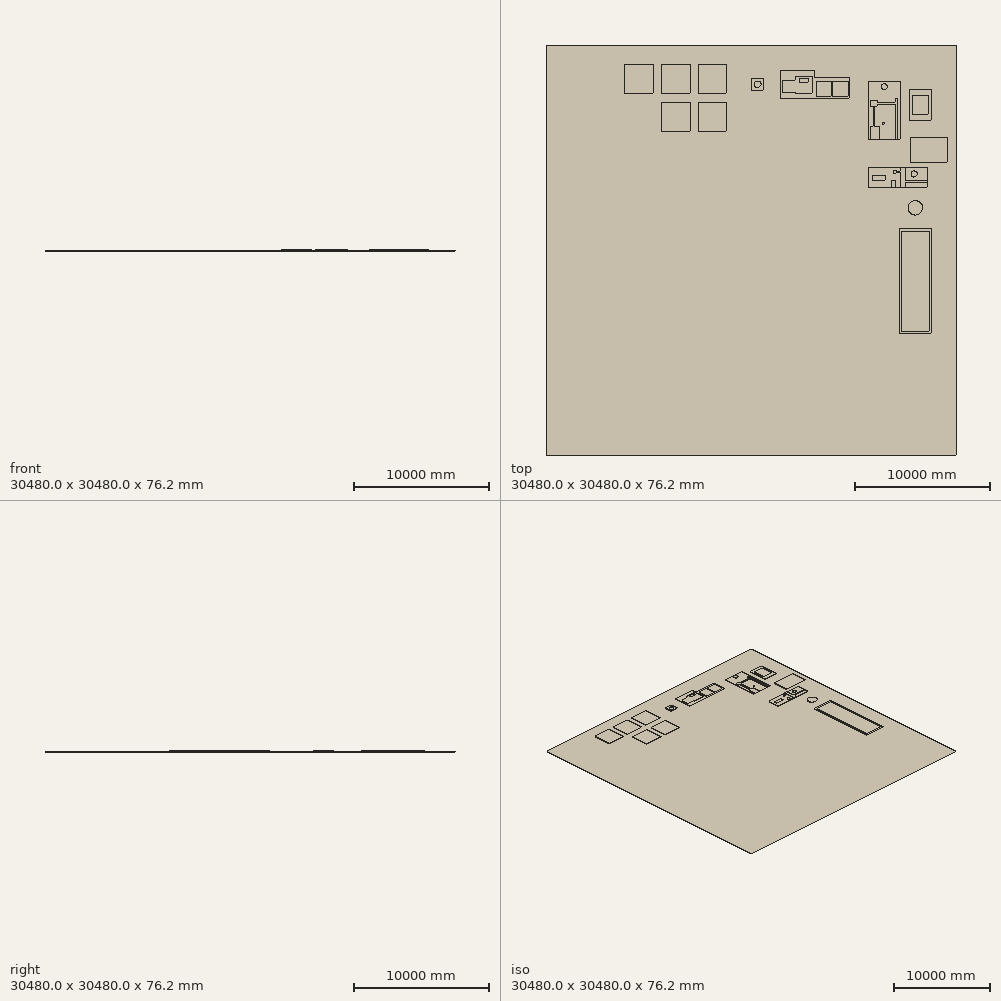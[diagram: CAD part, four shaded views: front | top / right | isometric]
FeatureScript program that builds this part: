
annotation { "Feature Type Name" : "Feature", "Feature Type Description" : "" }
export const myFeature = defineFeature(function(context is Context, id is Id, definition is map)
    precondition{}
    {
        {
            var Q0;
            Q0=qCreatedBy(makeId("Top.planeOp"),FACE);
            var sketch = newSketch(context, id + "F0", { "sketchPlane" : qUnion([Q0])});
            skLineSegment(sketch, "E0.bottom", {"start": v(15240, 15240) * mm, "end": v(-15240, 15240) * mm});
            skLineSegment(sketch, "E0.top", {"start": v(15240, -15240) * mm, "end": v(-15240, -15240) * mm});
            skLineSegment(sketch, "E0.left", {"start": v(15240, 15240) * mm, "end": v(15240, -15240) * mm});
            skLineSegment(sketch, "E0.right", {"start": v(-15240, 15240) * mm, "end": v(-15240, -15240) * mm});
            skPoint(sketch, "E0.middle", {"position": v(0, 0) * mm});
            skSolve(sketch);
        }
        {
            var Q0;
            Q0 = qSketchRegion(id + "F0", true);
            extrude(context, id + "F1", {"entities" : qUnion([Q0]), "depth" : 25.4 * mm, "offsetDistance" : 25.4 * mm});
        }
        {
            var Q0;
            Q0=makeQuery(id+"F1.opExtrude","CAP_FACE",FACE,{"disambiguationData":[OSD([sQuery(id+"F0.wireOp",EDGE,"E0.bottom"),sQuery(id+"F0.wireOp",EDGE,"E0.top"),sQuery(id+"F0.wireOp",EDGE,"E0.left"),sQuery(id+"F0.wireOp",EDGE,"E0.right")])],"isStart":false});
            var sketch = newSketch(context, id + "F2", { "sketchPlane" : qUnion([Q0])});
            skLineSegment(sketch, "E1.bottom", {"start": v(2133.6, 12852.4) * mm, "end": v(7315.2, 12852.4) * mm});
            skLineSegment(sketch, "E1.top", {"start": v(2133.6, 11277.6) * mm, "end": v(7315.2, 11277.6) * mm});
            skLineSegment(sketch, "E1.left", {"start": v(2133.6, 12852.4) * mm, "end": v(2133.6, 11277.6) * mm});
            skLineSegment(sketch, "E1.right", {"start": v(7315.2, 12852.4) * mm, "end": v(7315.2, 11277.6) * mm});
            skLineSegment(sketch, "E2.bottom", {"start": v(0, 12801.6) * mm, "end": v(914.4, 12801.6) * mm});
            skLineSegment(sketch, "E2.top", {"start": v(0, 11887.2) * mm, "end": v(914.4, 11887.2) * mm});
            skLineSegment(sketch, "E2.left", {"start": v(0, 12801.6) * mm, "end": v(0, 11887.2) * mm});
            skLineSegment(sketch, "E2.right", {"start": v(914.4, 12801.6) * mm, "end": v(914.4, 11887.2) * mm});
            skCircle(sketch, "E3", {"center": v(457.2, 12344.4) * mm, "radius": 254 * mm});
            skLineSegment(sketch, "E4.bottom", {"start": v(8661.4, 6146.8) * mm, "end": v(13106.4, 6146.8) * mm});
            skLineSegment(sketch, "E4.top", {"start": v(8661.4, 4699) * mm, "end": v(13106.4, 4699) * mm});
            skLineSegment(sketch, "E4.left", {"start": v(8661.4, 6146.8) * mm, "end": v(8661.4, 4699) * mm});
            skLineSegment(sketch, "E4.right", {"start": v(13106.4, 6146.8) * mm, "end": v(13106.4, 4699) * mm});
            skCircle(sketch, "E5", {"center": v(12192, 3161.27) * mm, "radius": 533.4 * mm});
            skLineSegment(sketch, "E6.bottom", {"start": v(10972.8, 1637.27) * mm, "end": v(13411.2, 1637.27) * mm});
            skLineSegment(sketch, "E6.top", {"start": v(10972.8, -6196.1) * mm, "end": v(13411.2, -6196.1) * mm});
            skLineSegment(sketch, "E6.left", {"start": v(10972.8, 1637.27) * mm, "end": v(10972.8, -6196.1) * mm});
            skLineSegment(sketch, "E6.right", {"start": v(13411.2, 1637.27) * mm, "end": v(13411.2, -6196.1) * mm});
            skLineSegment(sketch, "E7.bottom", {"start": v(2133.6, 12852.4) * mm, "end": v(4673.6, 12852.4) * mm});
            skLineSegment(sketch, "E7.top", {"start": v(2133.6, 13411.2) * mm, "end": v(4673.6, 13411.2) * mm});
            skLineSegment(sketch, "E7.left", {"start": v(2133.6, 12852.4) * mm, "end": v(2133.6, 13411.2) * mm});
            skLineSegment(sketch, "E7.right", {"start": v(4673.6, 12852.4) * mm, "end": v(4673.6, 13411.2) * mm});
            skLineSegment(sketch, "E8.bottom", {"start": v(11709.4, 11938) * mm, "end": v(13411.2, 11938) * mm});
            skLineSegment(sketch, "E8.top", {"start": v(11709.4, 9677.4) * mm, "end": v(13411.2, 9677.4) * mm});
            skLineSegment(sketch, "E8.left", {"start": v(11709.4, 11938) * mm, "end": v(11709.4, 9677.4) * mm});
            skLineSegment(sketch, "E8.right", {"start": v(13411.2, 11938) * mm, "end": v(13411.2, 9677.4) * mm});
            skLineSegment(sketch, "E9.bottom", {"start": v(8661.4, 12547.6) * mm, "end": v(11099.8, 12547.6) * mm});
            skLineSegment(sketch, "E9.top", {"start": v(8661.4, 8280.4) * mm, "end": v(11099.8, 8280.4) * mm});
            skLineSegment(sketch, "E9.left", {"start": v(8661.4, 12547.6) * mm, "end": v(8661.4, 8280.4) * mm});
            skLineSegment(sketch, "E9.right", {"start": v(11099.8, 12547.6) * mm, "end": v(11099.8, 8280.4) * mm});
            skLineSegment(sketch, "E10.bottom", {"start": v(-3962.4, 8839.2) * mm, "end": v(-3962.4, 10972.8) * mm});
            skLineSegment(sketch, "E10.top", {"start": v(-1828.8, 8839.2) * mm, "end": v(-1828.8, 10972.8) * mm});
            skLineSegment(sketch, "E10.left", {"start": v(-3962.4, 8839.2) * mm, "end": v(-1828.8, 8839.2) * mm});
            skLineSegment(sketch, "E10.right", {"start": v(-3962.4, 10972.8) * mm, "end": v(-1828.8, 10972.8) * mm});
            skLineSegment(sketch, "E11.bottom", {"start": v(-3962.4, 13839.55) * mm, "end": v(-1828.8, 13839.55) * mm});
            skLineSegment(sketch, "E11.top", {"start": v(-3962.4, 11705.95) * mm, "end": v(-1828.8, 11705.95) * mm});
            skLineSegment(sketch, "E11.left", {"start": v(-3962.4, 13839.55) * mm, "end": v(-3962.4, 11705.95) * mm});
            skLineSegment(sketch, "E11.right", {"start": v(-1828.8, 13839.55) * mm, "end": v(-1828.8, 11705.95) * mm});
            skLineSegment(sketch, "E12.bottom", {"start": v(-6705.6, 13839.55) * mm, "end": v(-4572, 13839.55) * mm});
            skLineSegment(sketch, "E12.top", {"start": v(-6705.6, 11705.95) * mm, "end": v(-4572, 11705.95) * mm});
            skLineSegment(sketch, "E12.left", {"start": v(-6705.6, 13839.55) * mm, "end": v(-6705.6, 11705.95) * mm});
            skLineSegment(sketch, "E12.right", {"start": v(-4572, 13839.55) * mm, "end": v(-4572, 11705.95) * mm});
            skLineSegment(sketch, "E13.bottom", {"start": v(-6705.6, 10972.8) * mm, "end": v(-4572, 10972.8) * mm});
            skLineSegment(sketch, "E13.top", {"start": v(-6705.6, 8839.2) * mm, "end": v(-4572, 8839.2) * mm});
            skLineSegment(sketch, "E13.left", {"start": v(-6705.6, 10972.8) * mm, "end": v(-6705.6, 8839.2) * mm});
            skLineSegment(sketch, "E13.right", {"start": v(-4572, 10972.8) * mm, "end": v(-4572, 8839.2) * mm});
            skLineSegment(sketch, "E14.bottom", {"start": v(-9448.8, 13819.2) * mm, "end": v(-7315.2, 13819.2) * mm});
            skLineSegment(sketch, "E14.top", {"start": v(-9448.8, 11685.6) * mm, "end": v(-7315.2, 11685.6) * mm});
            skLineSegment(sketch, "E14.left", {"start": v(-9448.8, 13819.2) * mm, "end": v(-9448.8, 11685.6) * mm});
            skLineSegment(sketch, "E14.right", {"start": v(-7315.2, 13819.2) * mm, "end": v(-7315.2, 11685.6) * mm});
            skLineSegment(sketch, "E15.bottom", {"start": v(11819.73, 8392.58) * mm, "end": v(14562.93, 8392.58) * mm});
            skLineSegment(sketch, "E15.top", {"start": v(11819.73, 6563.78) * mm, "end": v(14562.93, 6563.78) * mm});
            skLineSegment(sketch, "E15.left", {"start": v(11819.73, 8392.58) * mm, "end": v(11819.73, 6563.78) * mm});
            skLineSegment(sketch, "E15.right", {"start": v(14562.93, 8392.58) * mm, "end": v(14562.93, 6563.78) * mm});
            skSolve(sketch);
        }
        {
            var Q0;
            Q0 = qSketchRegion(id + "F2", true);
            extrude(context, id + "F3", {"entities" : qUnion([Q0]), "operationType" : NewBodyOperationType.ADD, "depth" : 25.4 * mm, "offsetDistance" : 25.4 * mm});
        }
        {
            var Q0;
            Q0=makeQuery(id+"F3.opExtrude","CAP_FACE",FACE,{"disambiguationData":[OSD([sQuery(id+"F2.wireOp",EDGE,"E1.bottom"),sQuery(id+"F2.wireOp",EDGE,"E1.top"),sQuery(id+"F2.wireOp",EDGE,"E1.left"),sQuery(id+"F2.wireOp",EDGE,"E1.right"),sQuery(id+"F2.wireOp",EDGE,"biDbiMLD-SDf2-hi3V-axfX-EiKsOqyBmbyk.top"),sQuery(id+"F2.wireOp",EDGE,"biDbiMLD-SDf2-hi3V-axfX-EiKsOqyBmbyk.left"),sQuery(id+"F2.wireOp",EDGE,"biDbiMLD-SDf2-hi3V-axfX-EiKsOqyBmbyk.right")])],"isStart":false});
            var sketch = newSketch(context, id + "F4", { "sketchPlane" : qUnion([Q0])});
            skPoint(sketch, "E16.centerSnap0", {"position": v(7315.2, 12065) * mm});
            skLineSegment(sketch, "E17.bottom", {"start": v(8991.6, 5588) * mm, "end": v(9956.8, 5588) * mm});
            skLineSegment(sketch, "E17.top", {"start": v(8991.6, 5207) * mm, "end": v(9956.8, 5207) * mm});
            skLineSegment(sketch, "E17.left", {"start": v(8991.6, 5588) * mm, "end": v(8991.6, 5207) * mm});
            skLineSegment(sketch, "E17.right", {"start": v(9956.8, 5588) * mm, "end": v(9956.8, 5207) * mm});
            skLineSegment(sketch, "E18.bottom", {"start": v(10566.4, 5969) * mm, "end": v(10769.6, 5969) * mm});
            skLineSegment(sketch, "E18.top", {"start": v(10566.4, 5689.6) * mm, "end": v(10769.6, 5689.6) * mm});
            skLineSegment(sketch, "E18.left", {"start": v(10566.4, 5969) * mm, "end": v(10566.4, 5689.6) * mm});
            skLineSegment(sketch, "E18.right", {"start": v(10769.6, 5969) * mm, "end": v(10769.6, 5689.6) * mm});
            skLineSegment(sketch, "E19.bottom", {"start": v(11074.4, 6146.8) * mm, "end": v(11455.4, 6146.8) * mm});
            skLineSegment(sketch, "E19.top", {"start": v(11074.4, 4699) * mm, "end": v(11455.4, 4699) * mm});
            skLineSegment(sketch, "E19.left", {"start": v(11074.4, 6146.8) * mm, "end": v(11074.4, 4699) * mm});
            skLineSegment(sketch, "E19.right", {"start": v(11455.4, 6146.8) * mm, "end": v(11455.4, 4699) * mm});
            skLineSegment(sketch, "E20.bottom", {"start": v(11455.4, 5054.6) * mm, "end": v(13106.4, 5054.6) * mm});
            skLineSegment(sketch, "E20.top", {"start": v(11455.4, 5207) * mm, "end": v(13106.4, 5207) * mm});
            skLineSegment(sketch, "E20.left", {"start": v(11455.4, 5054.6) * mm, "end": v(11455.4, 5207) * mm});
            skLineSegment(sketch, "E20.right", {"start": v(13106.4, 5054.6) * mm, "end": v(13106.4, 5207) * mm});
            skLineSegment(sketch, "E21.bottom", {"start": v(11074.4, 5791.2) * mm, "end": v(10769.6, 5791.2) * mm});
            skLineSegment(sketch, "E21.top", {"start": v(11074.4, 5892.8) * mm, "end": v(10769.6, 5892.8) * mm});
            skLineSegment(sketch, "E21.left", {"start": v(11074.4, 5791.2) * mm, "end": v(11074.4, 5892.8) * mm});
            skLineSegment(sketch, "E21.right", {"start": v(10769.6, 5791.2) * mm, "end": v(10769.6, 5892.8) * mm});
            skCircle(sketch, "E22", {"center": v(12090.4, 5689.6) * mm, "radius": 228.6 * mm});
            skLineSegment(sketch, "E23.bottom", {"start": v(10414, 4699) * mm, "end": v(10718.8, 4699) * mm});
            skLineSegment(sketch, "E23.top", {"start": v(10414, 5181.6) * mm, "end": v(10718.8, 5181.6) * mm});
            skLineSegment(sketch, "E23.left", {"start": v(10414, 4699) * mm, "end": v(10414, 5181.6) * mm});
            skLineSegment(sketch, "E23.right", {"start": v(10718.8, 4699) * mm, "end": v(10718.8, 5181.6) * mm});
            skLineSegment(sketch, "E24.bottom", {"start": v(2336.8, 12471.4) * mm, "end": v(3251.2, 12471.4) * mm});
            skLineSegment(sketch, "E24.top", {"start": v(2336.8, 11963.4) * mm, "end": v(3251.2, 11963.4) * mm});
            skLineSegment(sketch, "E24.left", {"start": v(2336.8, 12471.4) * mm, "end": v(2336.8, 11963.4) * mm});
            skLineSegment(sketch, "E24.right", {"start": v(3251.2, 12471.4) * mm, "end": v(3251.2, 11963.4) * mm});
            skLineSegment(sketch, "E25.bottom", {"start": v(3251.2, 12928.6) * mm, "end": v(4521.2, 12928.6) * mm});
            skLineSegment(sketch, "E25.top", {"start": v(3251.2, 11658.6) * mm, "end": v(4521.2, 11658.6) * mm});
            skLineSegment(sketch, "E25.left", {"start": v(3251.2, 12928.6) * mm, "end": v(3251.2, 11658.6) * mm});
            skLineSegment(sketch, "E25.right", {"start": v(4521.2, 12928.6) * mm, "end": v(4521.2, 11658.6) * mm});
            skLineSegment(sketch, "E26.bottom", {"start": v(3581.4, 12801.6) * mm, "end": v(4216.4, 12801.6) * mm});
            skLineSegment(sketch, "E26.top", {"start": v(3581.4, 12496.8) * mm, "end": v(4216.4, 12496.8) * mm});
            skLineSegment(sketch, "E26.left", {"start": v(3581.4, 12801.6) * mm, "end": v(3581.4, 12496.8) * mm});
            skLineSegment(sketch, "E26.right", {"start": v(4216.4, 12801.6) * mm, "end": v(4216.4, 12496.8) * mm});
            skLineSegment(sketch, "E27.bottom", {"start": v(2336.8, 12674.6) * mm, "end": v(3251.2, 12674.6) * mm});
            skLineSegment(sketch, "E27.top", {"start": v(2336.8, 11760.2) * mm, "end": v(3251.2, 11760.2) * mm});
            skLineSegment(sketch, "E27.left", {"start": v(2336.8, 12674.6) * mm, "end": v(2336.8, 11760.2) * mm});
            skLineSegment(sketch, "E27.right", {"start": v(3251.2, 12674.6) * mm, "end": v(3251.2, 11760.2) * mm});
            skLineSegment(sketch, "E28.bottom", {"start": v(11176, 1434.07) * mm, "end": v(13208, 1434.07) * mm});
            skLineSegment(sketch, "E28.top", {"start": v(11176, -5992.9) * mm, "end": v(13208, -5992.9) * mm});
            skLineSegment(sketch, "E28.left", {"start": v(11176, 1434.07) * mm, "end": v(11176, -5992.9) * mm});
            skLineSegment(sketch, "E28.right", {"start": v(13208, 1434.07) * mm, "end": v(13208, -5992.9) * mm});
            skLineSegment(sketch, "E29.bottom", {"start": v(4800.6, 12598.4) * mm, "end": v(5943.6, 12598.4) * mm});
            skLineSegment(sketch, "E29.top", {"start": v(4800.6, 11455.4) * mm, "end": v(5943.6, 11455.4) * mm});
            skLineSegment(sketch, "E29.left", {"start": v(4800.6, 12598.4) * mm, "end": v(4800.6, 11455.4) * mm});
            skLineSegment(sketch, "E29.right", {"start": v(5943.6, 12598.4) * mm, "end": v(5943.6, 11455.4) * mm});
            skLineSegment(sketch, "E30.bottom", {"start": v(6045.2, 12598.4) * mm, "end": v(7188.2, 12598.4) * mm});
            skLineSegment(sketch, "E30.top", {"start": v(6045.2, 11455.4) * mm, "end": v(7188.2, 11455.4) * mm});
            skLineSegment(sketch, "E30.left", {"start": v(6045.2, 12598.4) * mm, "end": v(6045.2, 11455.4) * mm});
            skLineSegment(sketch, "E30.right", {"start": v(7188.2, 12598.4) * mm, "end": v(7188.2, 11455.4) * mm});
            skLineSegment(sketch, "E31.bottom", {"start": v(11950.7, 11506.2) * mm, "end": v(13169.9, 11506.2) * mm});
            skLineSegment(sketch, "E31.top", {"start": v(11950.7, 10134.6) * mm, "end": v(13169.9, 10134.6) * mm});
            skLineSegment(sketch, "E31.left", {"start": v(11950.7, 11506.2) * mm, "end": v(11950.7, 10134.6) * mm});
            skLineSegment(sketch, "E31.right", {"start": v(13169.9, 11506.2) * mm, "end": v(13169.9, 10134.6) * mm});
            skLineSegment(sketch, "E32.bottom", {"start": v(8874.76, 8280.4) * mm, "end": v(9484.36, 8280.4) * mm});
            skLineSegment(sketch, "E32.top", {"start": v(8874.76, 9194.8) * mm, "end": v(9484.36, 9194.8) * mm});
            skLineSegment(sketch, "E32.left", {"start": v(8874.76, 8280.4) * mm, "end": v(8874.76, 9194.8) * mm});
            skLineSegment(sketch, "E32.right", {"start": v(9484.36, 8280.4) * mm, "end": v(9484.36, 9194.8) * mm});
            skPoint(sketch, "E33.oppositeSnap0", {"position": v(9179.56, 9194.8) * mm});
            skLineSegment(sketch, "E33.bottom", {"start": v(9057.64, 9194.8) * mm, "end": v(9179.56, 9194.8) * mm});
            skLineSegment(sketch, "E33.top", {"start": v(9057.64, 10718.8) * mm, "end": v(9179.56, 10718.8) * mm});
            skLineSegment(sketch, "E33.left", {"start": v(9057.64, 9194.8) * mm, "end": v(9057.64, 10718.8) * mm});
            skLineSegment(sketch, "E33.right", {"start": v(9179.56, 9194.8) * mm, "end": v(9179.56, 10718.8) * mm});
            skLineSegment(sketch, "E34.bottom", {"start": v(8874.76, 10718.8) * mm, "end": v(9331.96, 10718.8) * mm});
            skLineSegment(sketch, "E34.top", {"start": v(8874.76, 11176) * mm, "end": v(9331.96, 11176) * mm});
            skLineSegment(sketch, "E34.left", {"start": v(8874.76, 10718.8) * mm, "end": v(8874.76, 11176) * mm});
            skLineSegment(sketch, "E34.right", {"start": v(9331.96, 10718.8) * mm, "end": v(9331.96, 11176) * mm});
            skLineSegment(sketch, "E35.bottom", {"start": v(10673.08, 11328.4) * mm, "end": v(10886.44, 11328.4) * mm});
            skLineSegment(sketch, "E35.top", {"start": v(10673.08, 8280.4) * mm, "end": v(10886.44, 8280.4) * mm});
            skLineSegment(sketch, "E35.left", {"start": v(10673.08, 11328.4) * mm, "end": v(10673.08, 8280.4) * mm});
            skLineSegment(sketch, "E35.right", {"start": v(10886.44, 11328.4) * mm, "end": v(10886.44, 8280.4) * mm});
            skCircle(sketch, "E36", {"center": v(9880.6, 12166.6) * mm, "radius": 228.6 * mm});
            skLineSegment(sketch, "E37.bottom", {"start": v(9331.96, 11023.6) * mm, "end": v(10673.08, 11023.6) * mm});
            skLineSegment(sketch, "E37.top", {"start": v(9331.96, 10840.72) * mm, "end": v(10673.08, 10840.72) * mm});
            skLineSegment(sketch, "E37.left", {"start": v(9331.96, 11023.6) * mm, "end": v(9331.96, 10840.72) * mm});
            skLineSegment(sketch, "E37.right", {"start": v(10673.08, 11023.6) * mm, "end": v(10673.08, 10840.72) * mm});
            skLineSegment(sketch, "E38.bottom", {"start": v(9712.96, 9499.6) * mm, "end": v(9865.36, 9499.6) * mm});
            skLineSegment(sketch, "E38.top", {"start": v(9712.96, 9347.2) * mm, "end": v(9865.36, 9347.2) * mm});
            skLineSegment(sketch, "E38.left", {"start": v(9712.96, 9499.6) * mm, "end": v(9712.96, 9347.2) * mm});
            skLineSegment(sketch, "E38.right", {"start": v(9865.36, 9499.6) * mm, "end": v(9865.36, 9347.2) * mm});
            skSolve(sketch);
        }
        {
            var Q0;
            Q0 = qSketchRegion(id + "F4", true);
            extrude(context, id + "F5", {"entities" : qUnion([Q0]), "operationType" : NewBodyOperationType.ADD, "depth" : 25.4 * mm, "offsetDistance" : 25.4 * mm});
        }
    });
